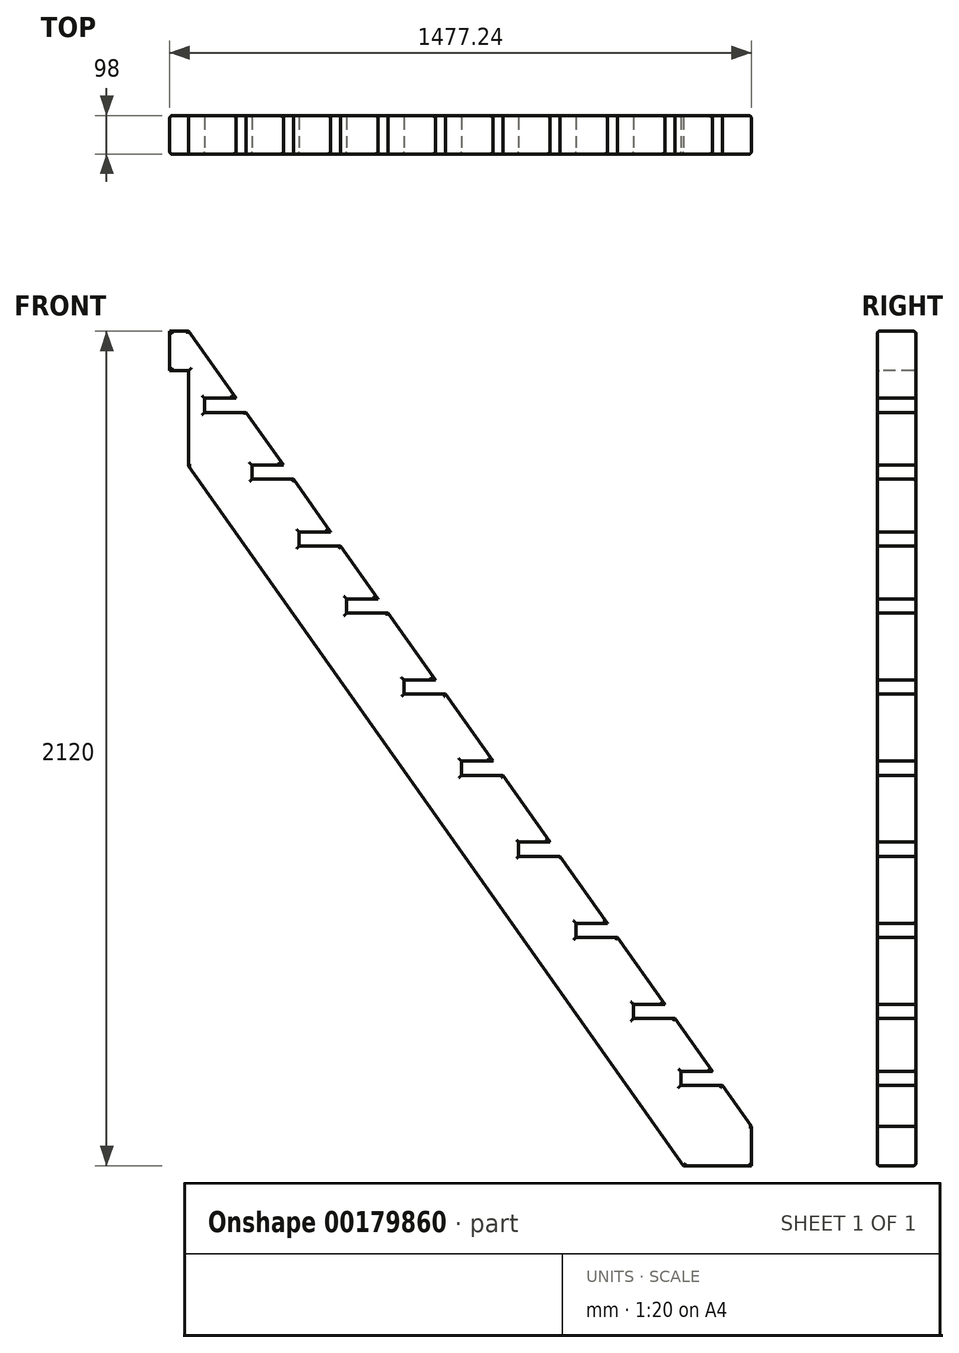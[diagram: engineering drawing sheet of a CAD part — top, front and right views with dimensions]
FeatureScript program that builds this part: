
annotation { "Feature Type Name" : "Feature", "Feature Type Description" : "" }
export const myFeature = defineFeature(function(context is Context, id is Id, definition is map)
    precondition{}
    {
        {
            var Q0;
            Q0=qCreatedBy(makeId("Front.planeOp"),FACE);
            var sketch = newSketch(context, id + "F0", { "sketchPlane" : qUnion([Q0])});
            skLineSegment(sketch, "E0", {"start": v(-837.22, 978.42) * mm, "end": v(662.78, -1141.58) * mm});
            skLineSegment(sketch, "E1", {"start": v(420.23, -1141.58) * mm, "end": v(-837.22, 635.62) * mm});
            skLineSegment(sketch, "E2", {"start": v(-837.22, 635.62) * mm, "end": v(-837.22, 978.42) * mm});
            skLineSegment(sketch, "E3", {"start": v(-716.94, 808.42) * mm, "end": v(-796.94, 808.42) * mm});
            skLineSegment(sketch, "E4", {"start": v(-796.94, 808.42) * mm, "end": v(-796.94, 772.42) * mm});
            skLineSegment(sketch, "E5", {"start": v(-796.94, 772.42) * mm, "end": v(-691.47, 772.42) * mm});
            skLineSegment(sketch, "E6", {"start": v(-596.66, 638.42) * mm, "end": v(-676.66, 638.42) * mm});
            skLineSegment(sketch, "E7", {"start": v(-676.66, 638.42) * mm, "end": v(-676.66, 602.42) * mm});
            skLineSegment(sketch, "E8", {"start": v(-676.66, 602.42) * mm, "end": v(-571.19, 602.42) * mm});
            skLineSegment(sketch, "E9", {"start": v(-476.37, 468.42) * mm, "end": v(-556.37, 468.42) * mm});
            skLineSegment(sketch, "E10", {"start": v(-556.37, 468.42) * mm, "end": v(-556.37, 432.42) * mm});
            skLineSegment(sketch, "E11", {"start": v(-556.37, 432.42) * mm, "end": v(-450.9, 432.42) * mm});
            skLineSegment(sketch, "E12", {"start": v(-450.9, 432.42) * mm, "end": v(-356.1, 298.42) * mm});
            skLineSegment(sketch, "E13", {"start": v(-356.1, 298.42) * mm, "end": v(-436.1, 298.42) * mm});
            skLineSegment(sketch, "E14", {"start": v(-436.1, 298.42) * mm, "end": v(-436.1, 262.42) * mm});
            skLineSegment(sketch, "E15", {"start": v(-436.1, 262.42) * mm, "end": v(-330.62, 262.42) * mm});
            skLineSegment(sketch, "E16", {"start": v(-210.34, 92.42) * mm, "end": v(-290.34, 92.42) * mm});
            skLineSegment(sketch, "E17", {"start": v(-290.34, 92.42) * mm, "end": v(-290.34, 56.42) * mm});
            skLineSegment(sketch, "E18", {"start": v(-290.34, 56.42) * mm, "end": v(-184.86, 56.42) * mm});
            skLineSegment(sketch, "E19", {"start": v(-64.58, -113.58) * mm, "end": v(-144.58, -113.58) * mm});
            skLineSegment(sketch, "E20", {"start": v(-144.58, -113.58) * mm, "end": v(-144.58, -149.58) * mm});
            skLineSegment(sketch, "E21", {"start": v(-144.58, -149.58) * mm, "end": v(-39.1, -149.58) * mm});
            skLineSegment(sketch, "E22", {"start": v(81.17, -319.58) * mm, "end": v(1.17, -319.58) * mm});
            skLineSegment(sketch, "E23", {"start": v(1.17, -319.58) * mm, "end": v(1.17, -355.58) * mm});
            skLineSegment(sketch, "E24", {"start": v(1.17, -355.58) * mm, "end": v(106.65, -355.58) * mm});
            skLineSegment(sketch, "E25", {"start": v(226.93, -525.58) * mm, "end": v(146.93, -525.58) * mm});
            skLineSegment(sketch, "E26", {"start": v(146.93, -525.58) * mm, "end": v(146.93, -561.58) * mm});
            skLineSegment(sketch, "E27", {"start": v(146.93, -561.58) * mm, "end": v(252.4, -561.58) * mm});
            skLineSegment(sketch, "E28", {"start": v(372.68, -731.58) * mm, "end": v(292.68, -731.58) * mm});
            skLineSegment(sketch, "E29", {"start": v(292.68, -731.58) * mm, "end": v(292.68, -767.58) * mm});
            skLineSegment(sketch, "E30", {"start": v(292.68, -767.58) * mm, "end": v(398.15, -767.58) * mm});
            skLineSegment(sketch, "E31", {"start": v(420.23, -1141.58) * mm, "end": v(662.78, -1141.58) * mm});
            skLineSegment(sketch, "E32", {"start": v(-837.22, 978.42) * mm, "end": v(-837.22, -1141.58) * mm, "construction": true});
            skLineSegment(sketch, "E33", {"start": v(-837.22, -1141.58) * mm, "end": v(662.78, -1141.58) * mm, "construction": true});
            skLineSegment(sketch, "E34", {"start": v(-837.22, 978.42) * mm, "end": v(-885.22, 978.42) * mm});
            skLineSegment(sketch, "E35", {"start": v(-885.22, 978.42) * mm, "end": v(-885.22, 878.42) * mm});
            skLineSegment(sketch, "E36", {"start": v(-885.22, 878.42) * mm, "end": v(-837.22, 878.42) * mm});
            skLineSegment(sketch, "E37", {"start": v(-796.94, 808.42) * mm, "end": v(-646.94, 808.42) * mm, "construction": true});
            skLineSegment(sketch, "E38", {"start": v(-646.94, 808.42) * mm, "end": v(-646.94, 772.42) * mm, "construction": true});
            skLineSegment(sketch, "E39", {"start": v(-646.94, 772.42) * mm, "end": v(-691.47, 772.42) * mm, "construction": true});
            skLineSegment(sketch, "E40", {"start": v(-646.94, 808.42) * mm, "end": v(-496.94, 808.42) * mm, "construction": true});
            skLineSegment(sketch, "E41", {"start": v(-496.94, 808.42) * mm, "end": v(-496.94, 772.42) * mm, "construction": true});
            skLineSegment(sketch, "E42", {"start": v(-496.94, 772.42) * mm, "end": v(-646.94, 772.42) * mm, "construction": true});
            skLineSegment(sketch, "E43", {"start": v(-676.66, 638.42) * mm, "end": v(-526.66, 638.42) * mm, "construction": true});
            skLineSegment(sketch, "E44", {"start": v(-526.66, 638.42) * mm, "end": v(-526.66, 602.42) * mm, "construction": true});
            skLineSegment(sketch, "E45", {"start": v(-571.19, 602.42) * mm, "end": v(-526.66, 602.42) * mm, "construction": true});
            skLineSegment(sketch, "E46", {"start": v(-526.66, 638.42) * mm, "end": v(-376.66, 638.42) * mm, "construction": true});
            skLineSegment(sketch, "E47", {"start": v(-376.66, 638.42) * mm, "end": v(-376.66, 602.42) * mm, "construction": true});
            skLineSegment(sketch, "E48", {"start": v(-376.66, 602.42) * mm, "end": v(-526.66, 602.42) * mm, "construction": true});
            skLineSegment(sketch, "E49", {"start": v(492.97, -901.58) * mm, "end": v(412.97, -901.58) * mm});
            skLineSegment(sketch, "E50", {"start": v(412.97, -901.58) * mm, "end": v(412.97, -937.58) * mm});
            skLineSegment(sketch, "E51", {"start": v(412.97, -937.58) * mm, "end": v(518.44, -937.58) * mm});
            skLineSegment(sketch, "E52", {"start": v(592.02, -1041.58) * mm, "end": v(592.02, -1141.58) * mm});
            skSolve(sketch);
        }
        {
            var Q0;
            Q0=makeQuery(id+"F0.imprint","IMPRINT",FACE,{"disambiguationData":[TD([[makeQuery(id+"F0.imprint","IMPRINT",EDGE,{"derivedFrom":sQuery(id+"F0.wireOp",EDGE,"E1")}),-1.0]])]});
            var Q1;
            {var subQ0=sQuery(id+"F0.wireOp",EDGE,"E34");Q1=makeQuery(id+"F0.imprint","IMPRINT",FACE,{"disambiguationData":[TD([[makeQuery(id+"F0.imprint","IMPRINT",EDGE,{"derivedFrom":subQ0}),1.0]])]});}
            extrude(context, id + "F1", {"entities" : qUnion([Q0, Q1]), "oppositeDirection" : true, "depth" : 98 * mm});
        }
        {
            var Q0;
            Q0=makeQuery(id+"F1.opExtrude","CAP_FACE",FACE,{"disambiguationData":[OSD([sQuery(id+"F0.wireOp",EDGE,"E0"),sQuery(id+"F0.wireOp",EDGE,"E1"),sQuery(id+"F0.wireOp",EDGE,"E2"),sQuery(id+"F0.wireOp",EDGE,"E3"),sQuery(id+"F0.wireOp",EDGE,"E4"),sQuery(id+"F0.wireOp",EDGE,"E5"),sQuery(id+"F0.wireOp",EDGE,"E6"),sQuery(id+"F0.wireOp",EDGE,"E7"),sQuery(id+"F0.wireOp",EDGE,"E8"),sQuery(id+"F0.wireOp",EDGE,"E9"),sQuery(id+"F0.wireOp",EDGE,"E10"),sQuery(id+"F0.wireOp",EDGE,"E11"),sQuery(id+"F0.wireOp",EDGE,"E12"),sQuery(id+"F0.wireOp",EDGE,"E13"),sQuery(id+"F0.wireOp",EDGE,"E14"),sQuery(id+"F0.wireOp",EDGE,"E15"),sQuery(id+"F0.wireOp",EDGE,"E16"),sQuery(id+"F0.wireOp",EDGE,"E17"),sQuery(id+"F0.wireOp",EDGE,"E18"),sQuery(id+"F0.wireOp",EDGE,"E19"),sQuery(id+"F0.wireOp",EDGE,"E20"),sQuery(id+"F0.wireOp",EDGE,"E21"),sQuery(id+"F0.wireOp",EDGE,"E22"),sQuery(id+"F0.wireOp",EDGE,"E23"),sQuery(id+"F0.wireOp",EDGE,"E24"),sQuery(id+"F0.wireOp",EDGE,"E25"),sQuery(id+"F0.wireOp",EDGE,"E26"),sQuery(id+"F0.wireOp",EDGE,"E27"),sQuery(id+"F0.wireOp",EDGE,"E28"),sQuery(id+"F0.wireOp",EDGE,"E29"),sQuery(id+"F0.wireOp",EDGE,"E30"),sQuery(id+"F0.wireOp",EDGE,"E31"),sQuery(id+"F0.wireOp",EDGE,"E34"),sQuery(id+"F0.wireOp",EDGE,"E35"),sQuery(id+"F0.wireOp",EDGE,"E36"),sQuery(id+"F0.wireOp",EDGE,"E49"),sQuery(id+"F0.wireOp",EDGE,"E50"),sQuery(id+"F0.wireOp",EDGE,"E51")])],"isStart":true});
            var Q1;
            Q1=makeQuery(id+"F1.opExtrude","CAP_FACE",FACE,{"disambiguationData":[OSD([sQuery(id+"F0.wireOp",EDGE,"E0"),sQuery(id+"F0.wireOp",EDGE,"E1"),sQuery(id+"F0.wireOp",EDGE,"E2"),sQuery(id+"F0.wireOp",EDGE,"E3"),sQuery(id+"F0.wireOp",EDGE,"E4"),sQuery(id+"F0.wireOp",EDGE,"E5"),sQuery(id+"F0.wireOp",EDGE,"E6"),sQuery(id+"F0.wireOp",EDGE,"E7"),sQuery(id+"F0.wireOp",EDGE,"E8"),sQuery(id+"F0.wireOp",EDGE,"E9"),sQuery(id+"F0.wireOp",EDGE,"E10"),sQuery(id+"F0.wireOp",EDGE,"E11"),sQuery(id+"F0.wireOp",EDGE,"E12"),sQuery(id+"F0.wireOp",EDGE,"E13"),sQuery(id+"F0.wireOp",EDGE,"E14"),sQuery(id+"F0.wireOp",EDGE,"E15"),sQuery(id+"F0.wireOp",EDGE,"E16"),sQuery(id+"F0.wireOp",EDGE,"E17"),sQuery(id+"F0.wireOp",EDGE,"E18"),sQuery(id+"F0.wireOp",EDGE,"E19"),sQuery(id+"F0.wireOp",EDGE,"E20"),sQuery(id+"F0.wireOp",EDGE,"E21"),sQuery(id+"F0.wireOp",EDGE,"E22"),sQuery(id+"F0.wireOp",EDGE,"E23"),sQuery(id+"F0.wireOp",EDGE,"E24"),sQuery(id+"F0.wireOp",EDGE,"E25"),sQuery(id+"F0.wireOp",EDGE,"E26"),sQuery(id+"F0.wireOp",EDGE,"E27"),sQuery(id+"F0.wireOp",EDGE,"E28"),sQuery(id+"F0.wireOp",EDGE,"E29"),sQuery(id+"F0.wireOp",EDGE,"E30"),sQuery(id+"F0.wireOp",EDGE,"E31"),sQuery(id+"F0.wireOp",EDGE,"E34"),sQuery(id+"F0.wireOp",EDGE,"E35"),sQuery(id+"F0.wireOp",EDGE,"E36"),sQuery(id+"F0.wireOp",EDGE,"E49"),sQuery(id+"F0.wireOp",EDGE,"E50"),sQuery(id+"F0.wireOp",EDGE,"E51")])],"isStart":false});
            fillet(context, id + "F2", {"entities" : qUnion([Q0, Q1]), "radius" : 6 * mm, "tangentPropagation" : true, "allowEdgeOverflow" : false});
        }
    });
